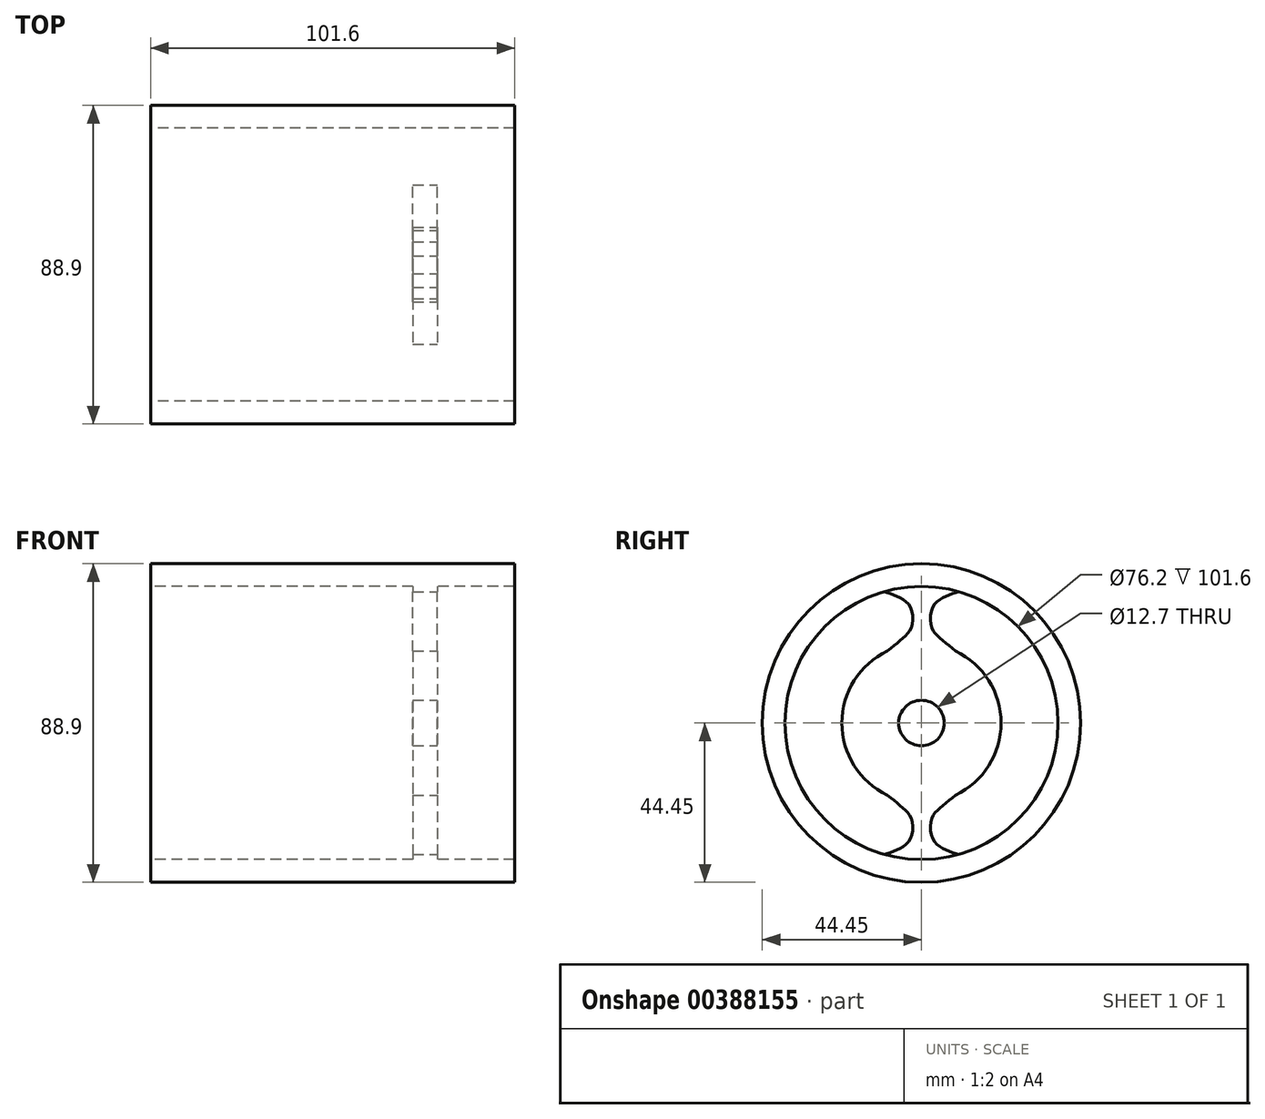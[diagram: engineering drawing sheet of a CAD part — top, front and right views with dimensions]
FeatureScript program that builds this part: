
annotation { "Feature Type Name" : "Feature", "Feature Type Description" : "" }
export const myFeature = defineFeature(function(context is Context, id is Id, definition is map)
    precondition{}
    {
        {
            var Q0;
            Q0=qCreatedBy(makeId("Front.planeOp"),FACE);
            var sketch = newSketch(context, id + "F0", { "sketchPlane" : qUnion([Q0])});
            skLineSegment(sketch, "E0.bottom", {"start": v(-80.05, 44.45) * mm, "end": v(21.55, 44.45) * mm});
            skLineSegment(sketch, "E0.top", {"start": v(-80.05, 38.1) * mm, "end": v(21.55, 38.1) * mm});
            skLineSegment(sketch, "E0.left", {"start": v(-80.05, 44.45) * mm, "end": v(-80.05, 38.1) * mm});
            skLineSegment(sketch, "E0.right", {"start": v(21.55, 44.45) * mm, "end": v(21.55, 38.1) * mm});
            skLineSegment(sketch, "E1", {"start": v(-76.63, 0) * mm, "end": v(0, 0) * mm, "construction": true});
            skSolve(sketch);
        }
        {
            var Q0;
            Q0 = qSketchRegion(id + "F0", true);
            var Q1;
            Q1=sQuery(id+"F0.wireOp",EDGE,"E1");
            revolve(context, id + "F1", {"entities" : qUnion([Q0]), "axis" : qUnion([Q1]), "revolveType" : RevolveType.FULL});
        }
        {
            var Q0;
            Q0=qCreatedBy(makeId("Right.planeOp"),FACE);
            var sketch = newSketch(context, id + "F2", { "sketchPlane" : qUnion([Q0])});
            skCircle(sketch, "E2", {"center": v(0, 0) * mm, "radius": 6.35 * mm});
            skCircle(sketch, "E3", {"center": v(0, 0) * mm, "radius": 22.23 * mm});
            skCircle(sketch, "E4.0", {"center": v(0, 0) * mm, "radius": 38.1 * mm});
            skFitSpline(sketch, "E5", {"points": [v(9.52, 20.08) * mm, v(5.16, 23.76) * mm, v(2.78, 26.86) * mm, v(3.26, 32.58) * mm, v(6.65, 35.28) * mm, v(10.42, 36.65) * mm], "startDerivative": vector(-21.51, 17.55) * mm, "endDerivative": vector(20.72, 5.07) * mm});
            skFitSpline(sketch, "E6.MirrorCS", {"points": [v(-9.52, 20.08) * mm, v(-5.16, 23.76) * mm, v(-2.78, 26.86) * mm, v(-3.26, 32.58) * mm, v(-6.65, 35.28) * mm, v(-10.42, 36.65) * mm], "startDerivative": vector(21.51, 17.55) * mm, "endDerivative": vector(-20.72, 5.07) * mm});
            skFitSpline(sketch, "E7.MirrorCS", {"points": [v(9.52, -20.08) * mm, v(5.16, -23.76) * mm, v(2.78, -26.86) * mm, v(3.26, -32.58) * mm, v(6.65, -35.28) * mm, v(10.42, -36.65) * mm], "startDerivative": vector(-21.51, -17.55) * mm, "endDerivative": vector(20.72, -5.07) * mm});
            skFitSpline(sketch, "E8.MirrorCS", {"points": [v(-9.52, -20.08) * mm, v(-5.16, -23.76) * mm, v(-2.78, -26.86) * mm, v(-3.26, -32.58) * mm, v(-6.65, -35.28) * mm, v(-10.42, -36.65) * mm], "startDerivative": vector(21.51, -17.55) * mm, "endDerivative": vector(-20.72, -5.07) * mm});
            skSolve(sketch);
        }
        {
            var Q0;
            {var subQ0=sQuery(id+"F2.wireOp",EDGE,"E5");Q0=makeQuery(id+"F2.imprint","IMPRINT",FACE,{"disambiguationData":[TD([[makeQuery(id+"F2.imprint","IMPRINT",EDGE,{"derivedFrom":subQ0}),1.0]])]});}
            var Q1;
            Q1=makeQuery(id+"F2.imprint","IMPRINT",FACE,{"disambiguationData":[TD([[makeQuery(id+"F2.imprint","IMPRINT",EDGE,{"derivedFrom":sQuery(id+"F2.wireOp",EDGE,"E2")}),-1.0]])]});
            var Q2;
            {var subQ0=sQuery(id+"F2.wireOp",EDGE,"E7.MirrorCS");Q2=makeQuery(id+"F2.imprint","IMPRINT",FACE,{"disambiguationData":[TD([[makeQuery(id+"F2.imprint","IMPRINT",EDGE,{"derivedFrom":subQ0}),-1.0]])]});}
            extrude(context, id + "F3", {"entities" : qUnion([Q0, Q1, Q2]), "operationType" : NewBodyOperationType.ADD, "oppositeDirection" : true, "depth" : 6.86 * mm});
        }
    });
